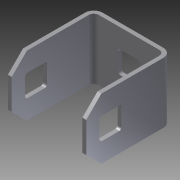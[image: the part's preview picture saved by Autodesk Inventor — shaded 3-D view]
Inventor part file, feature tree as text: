
AUTODESK INVENTOR PART (.ipt)
format: ipt  version: 2014 SP1 (Build 180222100, 222)  size: 313,856 bytes
history: native  units: in
note: dims shown in document units (in); Inventor stores cm internally (conversion verified against a paired STEP export)
features: sketch x8, extrude x6, projected_geometry x5, other x3, imported_body x1, fillet x1
ambient origin geometry x8: Origin, YZ Plane, XZ Plane, XY Plane, X Axis, Y Axis, Z Axis, Center Point
bodies: Body1 (feature_tree)
feature tree (24):
  parser-record x1  (decoder bookkeeping rows leaked as tree rows — omitted from the tree; the rows remain in map.json)
  imported_body  "Base1"
  extrude  "Extrusion1"  Depth=0.041in TaperAngle=90.0deg
  other  "Bend Part1"
  other  "Bend Part2"
  extrude  "Extrusion2"  Depth=0.041in TaperAngle=90.0deg
  extrude  "Extrusion3"  Depth=0.182in
  fillet  "Fillet1"  Radius=0.182in
  extrude  "Extrusion4"  Depth=2.0in TaperAngle=0.0deg
  extrude  "Extrusion5"  Depth=0.032in TaperAngle=0.0deg
  extrude  "Extrusion6"  Depth=0.109in
  sketch  "Sketch1"  dims[d0=1.0in d1=0.0in d2=0.041in d3=90.0deg]
  sketch  "Sketch2"  dims[d4=0.45in d5=0.041in d6=90.0deg]
  sketch  "Sketch3"  dims[d7=1.0in d8=0.25in d9=0.0in d10=0.0in d11=0.182in d12=0.182in]
  sketch  "Sketch4"  dims[d13=0.25in d14=2.0in d15=0.0in]
  projected_geometry  "Projected Loop1"
  projected_geometry  "Projected Loop2"
  projected_geometry  "Projected Loop3"
  projected_geometry  "Projected Loop4"
  projected_geometry  "Projected Loop5"
  sketch  "Sketch5"  dims[d16=0.02in d17=0.032in d18=0.0in]
  sketch  "Sketch6"  dims[d19=0.032in d20=0.0in d21=0.109in]
  sketch  "Sketch7"  dims[d22=0.25in]
  sketch  "Sketch8"  dims[d23=0.125in d24=135.0deg d25=135.0deg d26=2.0in d27=0.0in]
